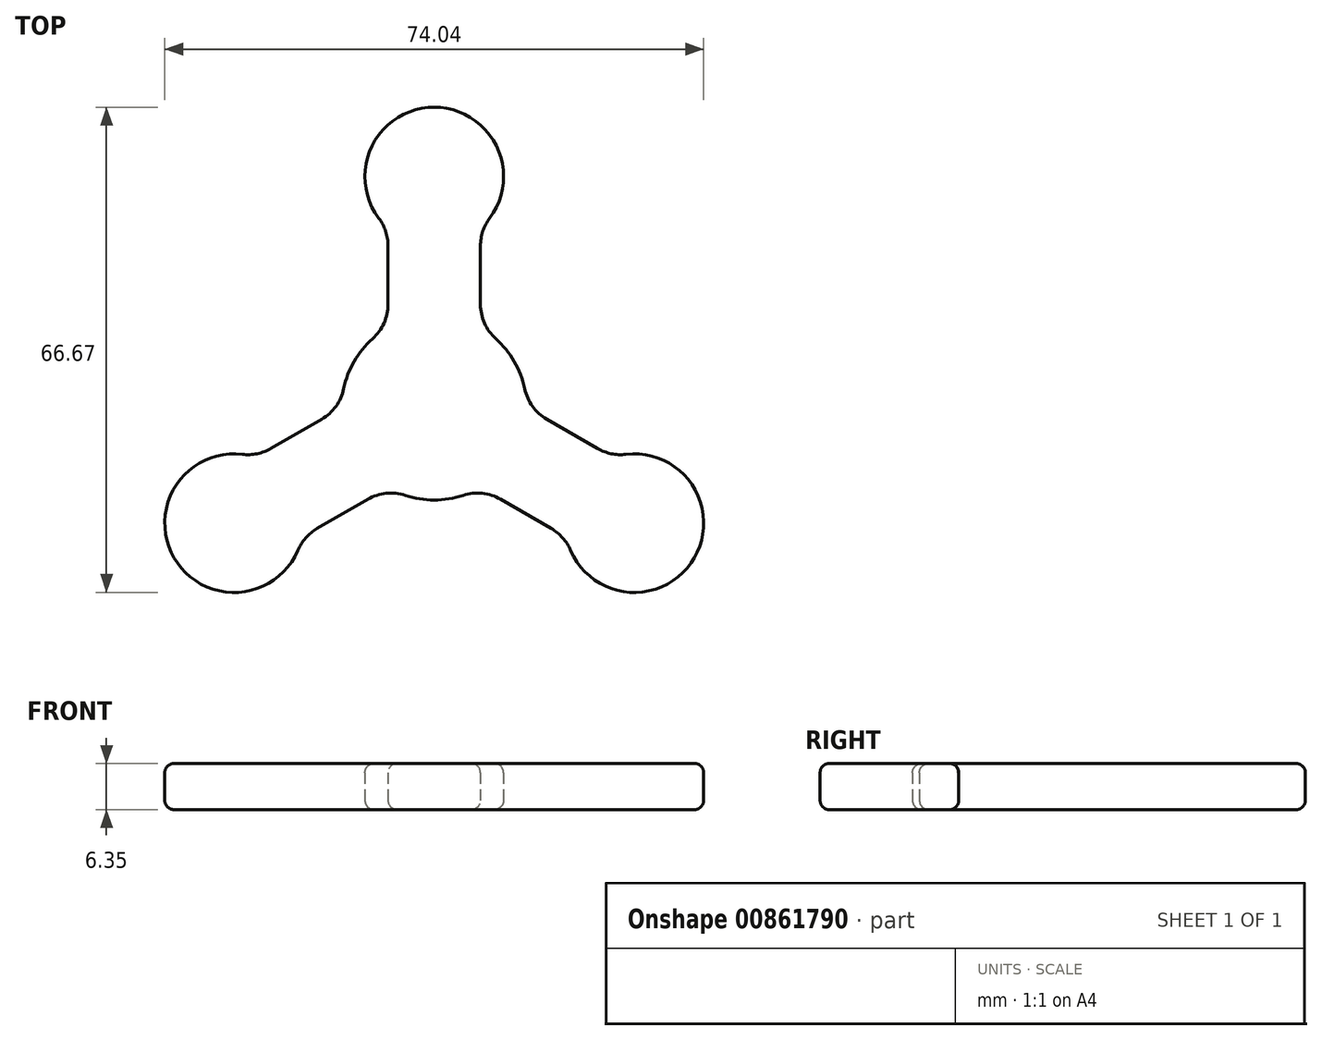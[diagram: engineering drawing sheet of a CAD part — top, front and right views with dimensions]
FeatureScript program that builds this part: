
annotation { "Feature Type Name" : "Feature", "Feature Type Description" : "" }
export const myFeature = defineFeature(function(context is Context, id is Id, definition is map)
    precondition{}
    {
        {
            var Q0;
            Q0=qCreatedBy(makeId("Top.planeOp"),FACE);
            var sketch = newSketch(context, id + "F0", { "sketchPlane" : qUnion([Q0])});
            skLineSegment(sketch, "E0", {"start": v(27.5, -15.88) * mm, "end": v(0, 0) * mm, "construction": true});
            skArc(sketch, "E1", {"start": v(7.62, 26.03) * mm, "mid": v(0, 41.27) * mm, "end": v(-7.62, 26.03) * mm});
            skArc(sketch, "E2", {"start": v(-26.36, -6.42) * mm, "mid": v(-35.75, -20.64) * mm, "end": v(-18.74, -19.62) * mm});
            skArc(sketch, "E3", {"start": v(18.74, -19.62) * mm, "mid": v(35.75, -20.64) * mm, "end": v(26.36, -6.42) * mm});
            skArc(sketch, "E4", {"start": v(-8.47, 9.47) * mm, "mid": v(-11, 6.35) * mm, "end": v(-12.43, 2.6) * mm});
            skLineSegment(sketch, "E5", {"start": v(-5.04, 18.56) * mm, "end": v(-5.04, 18.56) * mm});
            skLineSegment(sketch, "E6.0", {"start": v(6.35, 14.2) * mm, "end": v(6.35, 22.22) * mm});
            skLineSegment(sketch, "E7.0", {"start": v(-6.35, 14.2) * mm, "end": v(-6.35, 22.22) * mm});
            skLineSegment(sketch, "E8", {"start": v(0, 0) * mm, "end": v(0, 31.75) * mm, "construction": true});
            skLineSegment(sketch, "E9.0", {"start": v(-16.07, -16.61) * mm, "end": v(-9.12, -12.6) * mm});
            skLineSegment(sketch, "E10.0", {"start": v(-18.17, -17.82) * mm, "end": v(-6.35, -11) * mm});
            skLineSegment(sketch, "E11.0", {"start": v(-22.42, -5.61) * mm, "end": v(-15.47, -1.6) * mm});
            skArc(sketch, "E12.trimOffspring", {"start": v(-3.96, -12.07) * mm, "mid": v(0, -12.7) * mm, "end": v(3.96, -12.07) * mm});
            skLineSegment(sketch, "E13", {"start": v(0, 0) * mm, "end": v(-27.5, -15.87) * mm, "construction": true});
            skLineSegment(sketch, "E14.0", {"start": v(22.42, -5.61) * mm, "end": v(15.47, -1.6) * mm});
            skLineSegment(sketch, "E15.0", {"start": v(16.07, -16.61) * mm, "end": v(9.12, -12.6) * mm});
            skArc(sketch, "E16.trimOffspring", {"start": v(12.43, 2.6) * mm, "mid": v(11, 6.35) * mm, "end": v(8.47, 9.47) * mm});
            skPoint(sketch, "E17.visualSharp", {"position": v(-6.35, 11) * mm});
            skArc(sketch, "E17.filletArc", {"start": v(-8.47, 9.47) * mm, "mid": v(-6.9, 11.6) * mm, "end": v(-6.35, 14.2) * mm});
            skPoint(sketch, "E18.visualSharp", {"position": v(-6.35, 24.65) * mm});
            skArc(sketch, "E18.filletArc", {"start": v(-6.35, 22.22) * mm, "mid": v(-6.68, 24.23) * mm, "end": v(-7.62, 26.03) * mm});
            skPoint(sketch, "E19.visualSharp", {"position": v(6.35, 24.65) * mm});
            skArc(sketch, "E19.filletArc", {"start": v(7.62, 26.03) * mm, "mid": v(6.68, 24.23) * mm, "end": v(6.35, 22.22) * mm});
            skPoint(sketch, "E20.visualSharp", {"position": v(6.35, 11) * mm});
            skArc(sketch, "E20.filletArc", {"start": v(6.35, 14.2) * mm, "mid": v(6.9, 11.6) * mm, "end": v(8.47, 9.47) * mm});
            skPoint(sketch, "E21.visualSharp", {"position": v(12.7, 0) * mm});
            skArc(sketch, "E21.filletArc", {"start": v(12.43, 2.6) * mm, "mid": v(13.5, 0.18) * mm, "end": v(15.47, -1.6) * mm});
            skPoint(sketch, "E22.visualSharp", {"position": v(24.52, -6.83) * mm});
            skArc(sketch, "E22.filletArc", {"start": v(22.42, -5.61) * mm, "mid": v(24.32, -6.34) * mm, "end": v(26.36, -6.42) * mm});
            skPoint(sketch, "E23.visualSharp", {"position": v(18.17, -17.82) * mm});
            skArc(sketch, "E23.filletArc", {"start": v(18.74, -19.62) * mm, "mid": v(17.65, -17.9) * mm, "end": v(16.07, -16.61) * mm});
            skPoint(sketch, "E24.visualSharp", {"position": v(6.35, -11) * mm});
            skArc(sketch, "E24.filletArc", {"start": v(9.12, -12.6) * mm, "mid": v(6.6, -11.78) * mm, "end": v(3.96, -12.07) * mm});
            skPoint(sketch, "E25.visualSharp", {"position": v(-6.35, -11) * mm});
            skArc(sketch, "E25.filletArc", {"start": v(-3.96, -12.07) * mm, "mid": v(-6.6, -11.78) * mm, "end": v(-9.12, -12.6) * mm});
            skPoint(sketch, "E26.visualSharp", {"position": v(-18.17, -17.82) * mm});
            skArc(sketch, "E26.filletArc", {"start": v(-16.07, -16.61) * mm, "mid": v(-17.65, -17.9) * mm, "end": v(-18.74, -19.62) * mm});
            skPoint(sketch, "E27.visualSharp", {"position": v(-24.52, -6.83) * mm});
            skArc(sketch, "E27.filletArc", {"start": v(-26.36, -6.42) * mm, "mid": v(-24.32, -6.34) * mm, "end": v(-22.42, -5.61) * mm});
            skPoint(sketch, "E28.visualSharp", {"position": v(-12.7, 0) * mm});
            skArc(sketch, "E28.filletArc", {"start": v(-15.47, -1.6) * mm, "mid": v(-13.5, 0.18) * mm, "end": v(-12.43, 2.6) * mm});
            skSolve(sketch);
        }
        {
            var Q0;
            Q0=makeQuery(id+"F0.imprint","IMPRINT",FACE,{"disambiguationData":[TD([[makeQuery(id+"F0.imprint","IMPRINT",EDGE,{"derivedFrom":sQuery(id+"F0.wireOp",EDGE,"E1")}),1.0]])]});
            extrude(context, id + "F1", {"entities" : qUnion([Q0]), "depth" : 6.35 * mm, "offsetDistance" : 25.4 * mm});
        }
        {
            var Q0;
            Q0=makeQuery(id+"F1.opExtrude","CAP_EDGE",EDGE,{"disambiguationData":[OSD([sQuery(id+"F0.wireOp",EDGE,"E2")])],"isStart":false});
            var Q1;
            Q1=makeQuery(id+"F1.opExtrude","CAP_EDGE",EDGE,{"disambiguationData":[OSD([sQuery(id+"F0.wireOp",EDGE,"E2")])],"isStart":true});
            fillet(context, id + "F2", {"entities" : qUnion([Q0, Q1]), "radius" : 1.27 * mm, "tangentPropagation" : true, "allowEdgeOverflow" : false});
        }
    });
